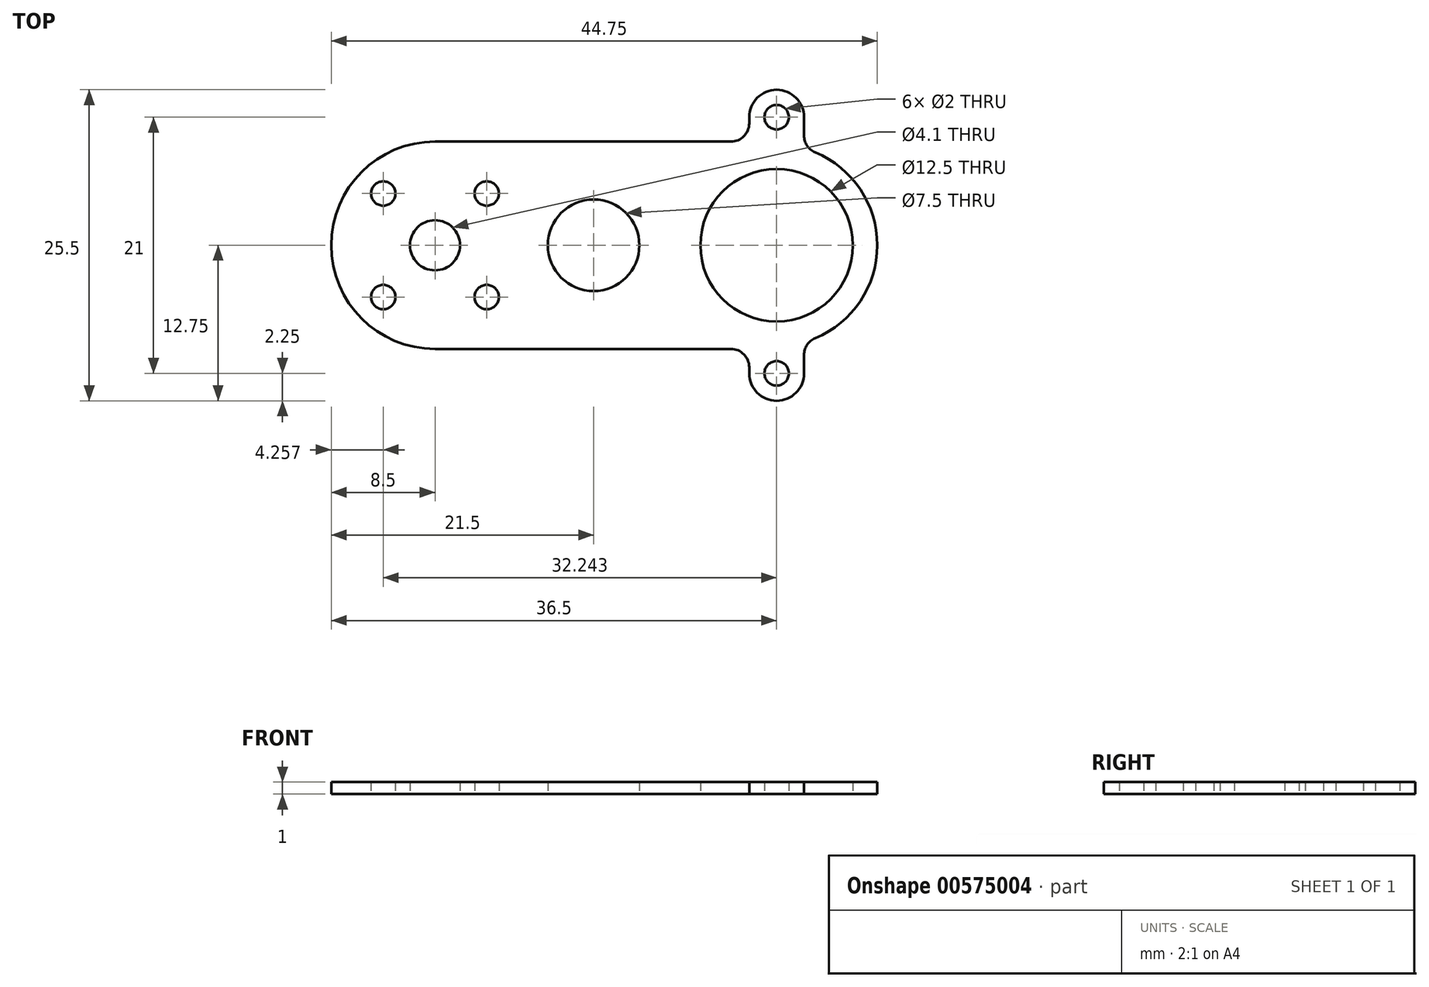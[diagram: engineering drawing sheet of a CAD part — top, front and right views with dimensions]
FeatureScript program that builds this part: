
annotation { "Feature Type Name" : "Feature", "Feature Type Description" : "" }
export const myFeature = defineFeature(function(context is Context, id is Id, definition is map)
    precondition{}
    {
        {
            var Q0;
            Q0=qCreatedBy(makeId("Top.planeOp"),FACE);
            var sketch = newSketch(context, id + "F0", { "sketchPlane" : qUnion([Q0])});
            skCircle(sketch, "E0", {"center": v(14, 0) * mm, "radius": 6.25 * mm});
            skLineSegment(sketch, "E1.bottom", {"start": v(-18.24, 4.24) * mm, "end": v(-9.76, 4.24) * mm, "construction": true});
            skLineSegment(sketch, "E1.top", {"start": v(-18.24, -4.24) * mm, "end": v(-9.76, -4.24) * mm, "construction": true});
            skLineSegment(sketch, "E1.left", {"start": v(-18.24, 4.24) * mm, "end": v(-18.24, -4.24) * mm, "construction": true});
            skLineSegment(sketch, "E1.right", {"start": v(-9.76, 4.24) * mm, "end": v(-9.76, -4.24) * mm, "construction": true});
            skPoint(sketch, "E1.middle", {"position": v(-14, 0) * mm});
            skLineSegment(sketch, "E2", {"start": v(-14, 0) * mm, "end": v(14, 0) * mm, "construction": true});
            skLineSegment(sketch, "E3", {"start": v(14, 0) * mm, "end": v(14, 10.5) * mm, "construction": true});
            skLineSegment(sketch, "E4", {"start": v(14, 10.5) * mm, "end": v(35, 10.5) * mm, "construction": true});
            skCircle(sketch, "E5", {"center": v(14, 10.5) * mm, "radius": 1 * mm});
            skCircle(sketch, "E6", {"center": v(35, 10.5) * mm, "radius": 1 * mm});
            skCircle(sketch, "E7.MirrorC", {"center": v(14, -10.5) * mm, "radius": 1 * mm});
            skCircle(sketch, "E8.MirrorC", {"center": v(35, -10.5) * mm, "radius": 1 * mm});
            skCircle(sketch, "E9", {"center": v(-14, 0) * mm, "radius": 2.05 * mm});
            skArc(sketch, "E10", {"start": v(11.75, 7.94) * mm, "mid": v(5.75, 0) * mm, "end": v(11.75, -7.94) * mm, "construction": true});
            skArc(sketch, "E11", {"start": v(16.25, 10.5) * mm, "mid": v(14, 12.75) * mm, "end": v(11.75, 10.5) * mm});
            skCircle(sketch, "E12", {"center": v(35, 10.5) * mm, "radius": 2.25 * mm});
            skArc(sketch, "E13.MirrorC", {"start": v(16.25, -10.5) * mm, "mid": v(14, -12.75) * mm, "end": v(11.75, -10.5) * mm});
            skCircle(sketch, "E14.MirrorC", {"center": v(35, -10.5) * mm, "radius": 2.25 * mm});
            skLineSegment(sketch, "E15", {"start": v(16.25, 10.5) * mm, "end": v(16.25, 9) * mm});
            skLineSegment(sketch, "E16.MirrorCS", {"start": v(11.75, 10.5) * mm, "end": v(11.75, 10) * mm});
            skLineSegment(sketch, "E17.MirrorCS", {"start": v(11.75, -10.5) * mm, "end": v(11.75, -10) * mm});
            skLineSegment(sketch, "E18.MirrorCS", {"start": v(16.25, -10.5) * mm, "end": v(16.25, -9) * mm});
            skArc(sketch, "E19.trimOffspring", {"start": v(17.17, -7.62) * mm, "mid": v(22.25, 0) * mm, "end": v(17.17, 7.62) * mm});
            skCircle(sketch, "E20", {"center": v(-14, 0) * mm, "radius": 6 * mm, "construction": true});
            skCircle(sketch, "E21", {"center": v(-18.24, 4.24) * mm, "radius": 1 * mm});
            skCircle(sketch, "E22.1.0", {"center": v(-18.24, -4.24) * mm, "radius": 1 * mm});
            skCircle(sketch, "E22.2.0", {"center": v(-9.76, -4.24) * mm, "radius": 1 * mm});
            skCircle(sketch, "E23.1.3.0", {"center": v(-9.76, 4.24) * mm, "radius": 1 * mm});
            skArc(sketch, "E24", {"start": v(-14, 8.5) * mm, "mid": v(-22.5, 0) * mm, "end": v(-14, -8.5) * mm});
            skLineSegment(sketch, "E25", {"start": v(-14, 8.5) * mm, "end": v(10.25, 8.5) * mm});
            skPoint(sketch, "E25.startSnap0", {"position": v(-14, 4.24) * mm});
            skLineSegment(sketch, "E26.MirrorCS", {"start": v(-14, -8.5) * mm, "end": v(10.25, -8.5) * mm});
            skPoint(sketch, "E27.newPointA", {"position": v(11.75, 8.5) * mm});
            skPoint(sketch, "E27.newPointB", {"position": v(11.75, 7.94) * mm});
            skArc(sketch, "E27.filletArc", {"start": v(10.25, 8.5) * mm, "mid": v(11.31, 8.94) * mm, "end": v(11.75, 10) * mm});
            skPoint(sketch, "E28.newPointA", {"position": v(11.75, -8.5) * mm});
            skPoint(sketch, "E28.newPointB", {"position": v(11.75, -7.94) * mm});
            skArc(sketch, "E28.filletArc", {"start": v(11.75, -10) * mm, "mid": v(11.31, -8.94) * mm, "end": v(10.25, -8.5) * mm});
            skPoint(sketch, "E29.visualSharp", {"position": v(16.25, 7.94) * mm});
            skArc(sketch, "E29.filletArc", {"start": v(16.25, 9) * mm, "mid": v(16.5, 8.17) * mm, "end": v(17.17, 7.62) * mm});
            skPoint(sketch, "E30.visualSharp", {"position": v(16.25, -7.94) * mm});
            skArc(sketch, "E30.filletArc", {"start": v(17.17, -7.62) * mm, "mid": v(16.5, -8.17) * mm, "end": v(16.25, -9) * mm});
            skCircle(sketch, "E31", {"center": v(-1, 0) * mm, "radius": 3.75 * mm});
            skSolve(sketch);
        }
        {
            var Q0;
            Q0=makeQuery(id+"F0.imprint","IMPRINT",FACE,{"disambiguationData":[TD([[makeQuery(id+"F0.imprint","IMPRINT",EDGE,{"derivedFrom":sQuery(id+"F0.wireOp",EDGE,"E0")}),-1.0]])]});
            extrude(context, id + "F1", {"entities" : qUnion([Q0]), "depth" : 1 * mm, "offsetDistance" : 25 * mm});
        }
    });
